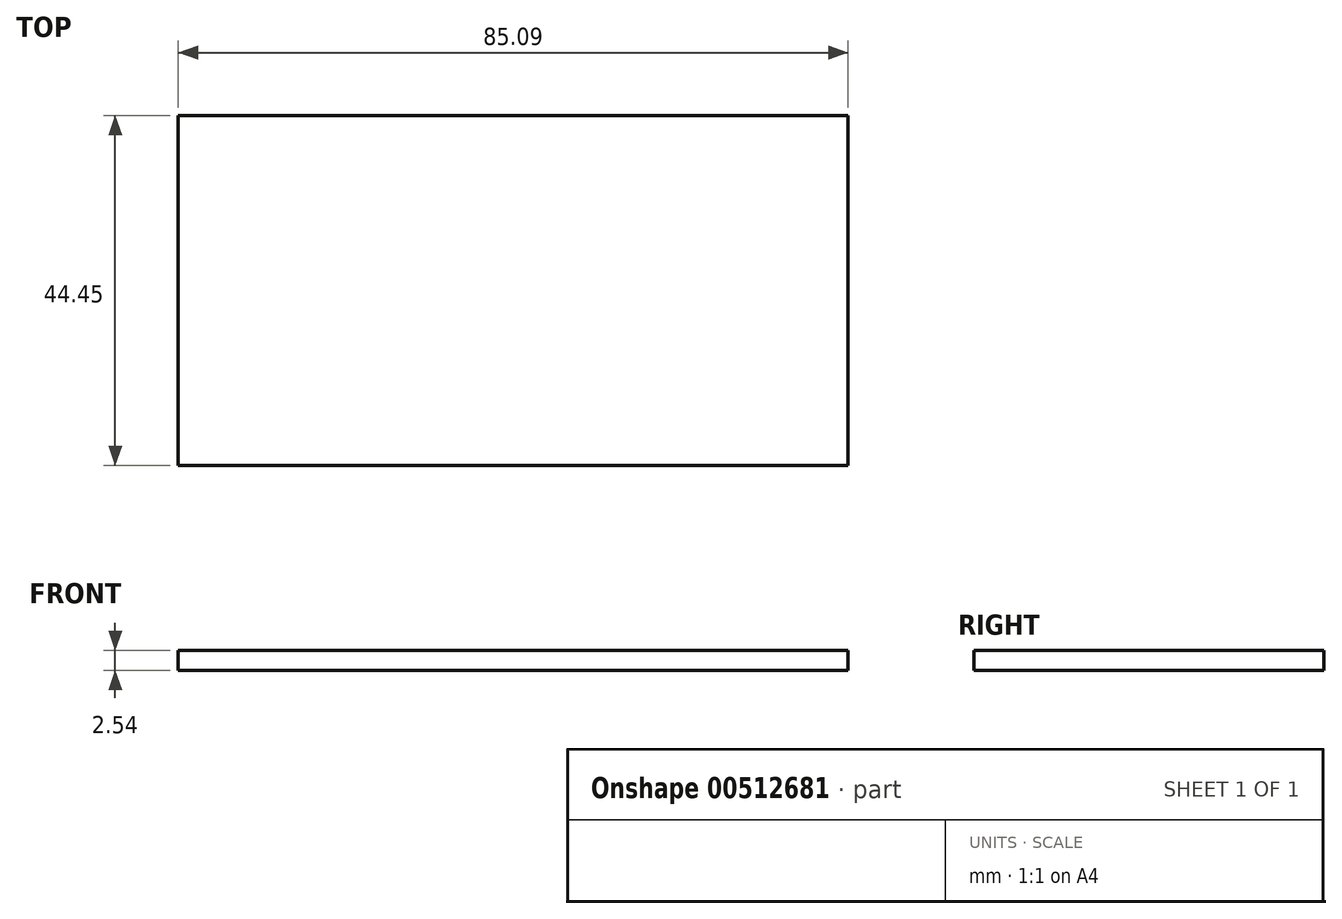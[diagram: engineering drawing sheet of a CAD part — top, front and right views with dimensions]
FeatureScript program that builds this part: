
annotation { "Feature Type Name" : "Feature", "Feature Type Description" : "" }
export const myFeature = defineFeature(function(context is Context, id is Id, definition is map)
    precondition{}
    {
        {
            var Q0;
            Q0=qCreatedBy(makeId("Top.planeOp"),FACE);
            var sketch = newSketch(context, id + "F0", { "sketchPlane" : qUnion([Q0])});
            skLineSegment(sketch, "E0.bottom", {"start": v(0, -9.67) * mm, "end": v(85.1, -9.67) * mm});
            skLineSegment(sketch, "E0.top", {"start": v(0, -54.12) * mm, "end": v(85.1, -54.12) * mm});
            skLineSegment(sketch, "E0.left", {"start": v(0, -9.67) * mm, "end": v(0, -54.12) * mm});
            skLineSegment(sketch, "E0.right", {"start": v(85.1, -9.67) * mm, "end": v(85.1, -54.12) * mm});
            skSolve(sketch);
        }
        {
            var Q0;
            Q0 = qSketchRegion(id + "F0", true);
            extrude(context, id + "F1", {"entities" : qUnion([Q0]), "depth" : 2.54 * mm});
        }
    });
